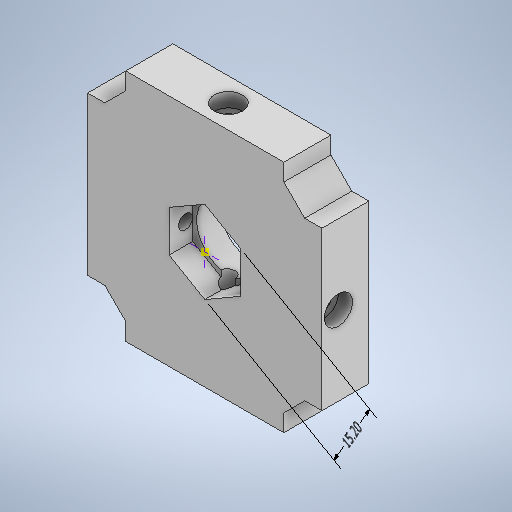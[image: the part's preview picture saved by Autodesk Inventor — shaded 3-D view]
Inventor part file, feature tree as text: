
AUTODESK INVENTOR PART (.ipt)
format: ipt  version: 2025 (Build 290162000, 162)  size: 304,128 bytes
history: native  units: mm
features: sketch x8, hole x4, extrude x2, other x1
ambient origin geometry x8: Origin, YZ Plane, XZ Plane, XY Plane, X Axis, Y Axis, Z Axis, Center Point
bodies: 实体1 (feature_tree)
feature tree (15):
  extrude  "拉伸1"  Depth=15.2mm
  sketch  "草图2"  dims[d31=5.0mm d32=0.0mm]
  sketch  "草图3"  dims[d33=13.5mm d34=6.0mm d35=4.0mm d36=2.0mm d37=90.0deg d38=0.5mm d39=20.594885mm]
  extrude  "拉伸2"  Depth=20.594885mm
  hole  "孔1"  [1 undecoded]
  hole  "孔2"  [1 undecoded]
  hole  "孔3"  [1 undecoded]
  hole  "孔4"  [1 undecoded]
  sketch  "草图1"  dims[d26=5.0mm d27=5.0mm d28=0.0mm d29=0.0mm d30=15.2mm]
  sketch  "草图4"  dims[d40=2.98mm d41=6.0mm d42=6.0mm d43=3.0mm d44=90.0deg d45=8.0mm d46=20.594885mm]
  sketch  "草图5"  dims[d47=2.98mm d48=6.0mm d49=6.0mm d50=3.0mm d51=90.0deg d52=8.0mm d53=20.594885mm]
  sketch  "草图6"  dims[d54=3.0mm d55=6.0mm d56=6.0mm d57=3.0mm d58=90.0deg d59=8.0mm d60=20.594885mm d61=15.2mm]
  sketch  "草图7"  dims[d62=5.873675mm d63=6.026246mm d64=15.2mm d65=0.25mm]
  sketch  "草图8"  dims[d66=0.375mm d67=14.3117mm d68=0.75mm d69=20.594885mm d70=0.0625mm d71=0.75mm d72=0.375mm]
  other  "线性尺寸 1"
note: 4 required parameter values undecoded (feature->parameter linkage not recoverable at this tier; creation-order binding heuristic only, values carry confidence <= 0.55)
